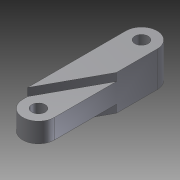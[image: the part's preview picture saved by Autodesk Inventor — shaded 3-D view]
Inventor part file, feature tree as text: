
AUTODESK INVENTOR PART (.ipt)
format: ipt  version: 2011 SP2 (Build 150309200, 309)  size: 101,888 bytes
history: native  units: mm
features: sketch x2, extrude x2, hole x1, projected_geometry x1
ambient origin geometry x8: Origin, YZ Plane, XZ Plane, XY Plane, X Axis, Y Axis, Z Axis, Center Point
bodies: Solid1 (feature_tree)
feature tree (6):
  sketch  "Sketch1"  dims[d0=4.0mm d6=26.268959mm]
  extrude  "Extrusion1"  Depth=26.268959mm
  extrude  "Extrusion2"  Depth=5.0mm TaperAngle=0.0deg
  hole  "Hole1"  [1 undecoded]
  sketch  "Sketch2"  dims[d14=9.0mm d15=0.0mm d16=3.4mm d17=6.0mm d18=4.4mm d19=3.0mm d20=90.0deg d21=8.0mm d22=20.594885mm d23=5.0mm d24=0.0mm]
  projected_geometry  "Projected Loop1"
note: 1 required parameter value undecoded (feature->parameter linkage not recoverable at this tier; creation-order binding heuristic only, values carry confidence <= 0.55)
